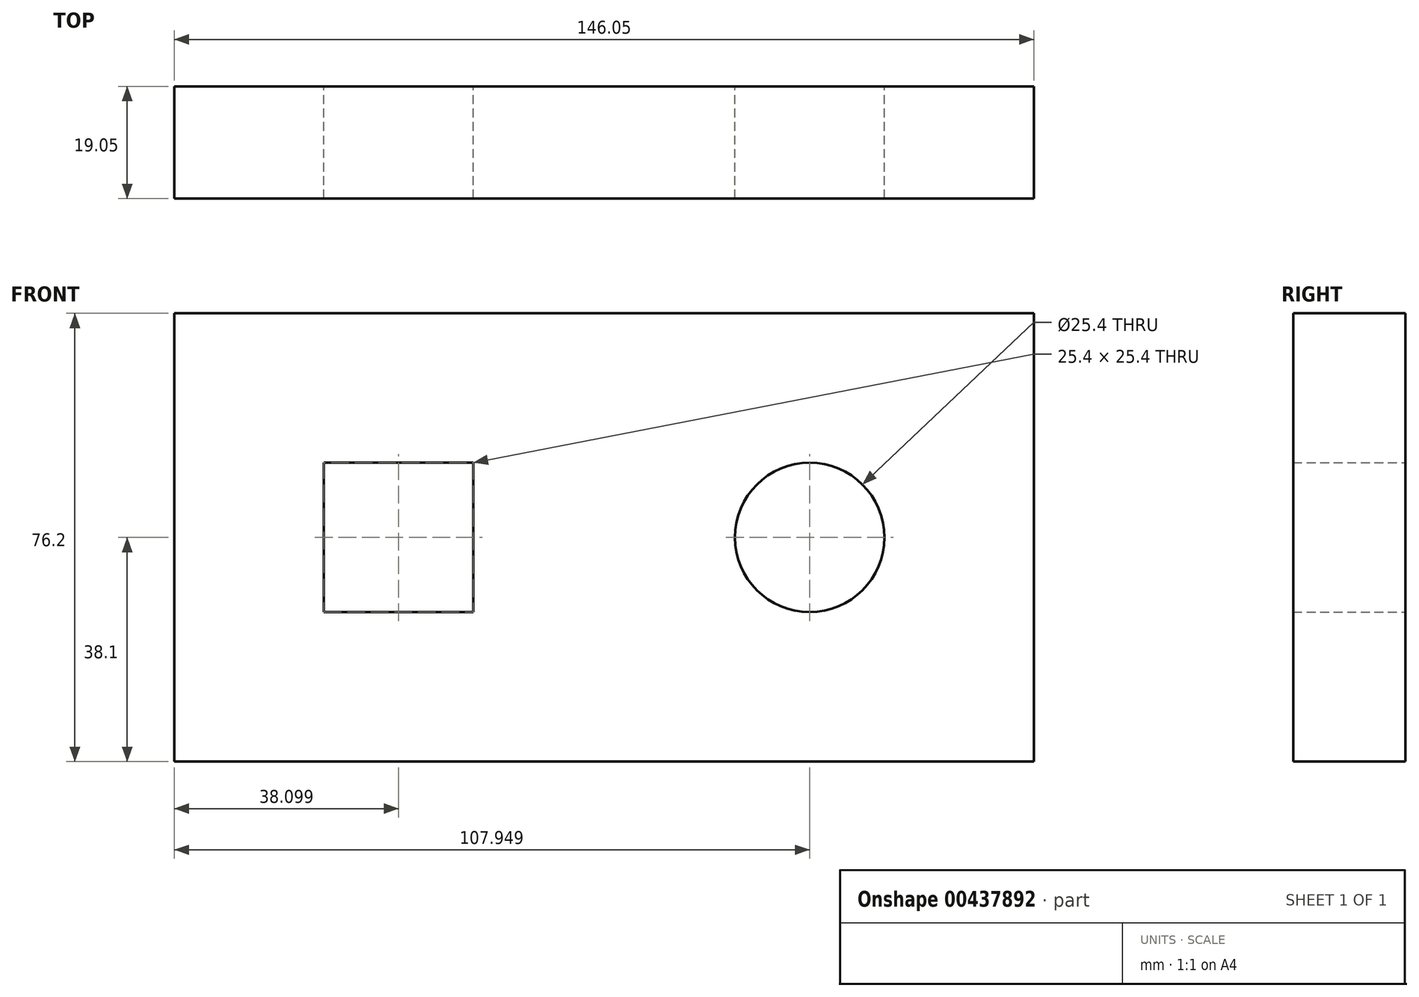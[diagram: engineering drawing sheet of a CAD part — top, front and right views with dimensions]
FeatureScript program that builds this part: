
annotation { "Feature Type Name" : "Feature", "Feature Type Description" : "" }
export const myFeature = defineFeature(function(context is Context, id is Id, definition is map)
    precondition{}
    {
        {
            var Q0;
            Q0=qCreatedBy(makeId("Front.planeOp"),FACE);
            var sketch = newSketch(context, id + "F0", { "sketchPlane" : qUnion([Q0])});
            skLineSegment(sketch, "E0", {"start": v(-64.16, 56.15) * mm, "end": v(-64.16, -20.05) * mm});
            skLineSegment(sketch, "E1", {"start": v(-64.16, 56.15) * mm, "end": v(81.89, 56.15) * mm});
            skLineSegment(sketch, "E2", {"start": v(81.89, 56.15) * mm, "end": v(81.89, -20.05) * mm});
            skLineSegment(sketch, "E3", {"start": v(81.89, -20.05) * mm, "end": v(-64.16, -20.05) * mm});
            skCircle(sketch, "E4", {"center": v(43.79, 18.05) * mm, "radius": 12.7 * mm});
            skLineSegment(sketch, "E5.bottom", {"start": v(-38.76, 30.75) * mm, "end": v(-13.36, 30.75) * mm});
            skLineSegment(sketch, "E5.top", {"start": v(-38.76, 5.35) * mm, "end": v(-13.36, 5.35) * mm});
            skLineSegment(sketch, "E5.left", {"start": v(-38.76, 30.75) * mm, "end": v(-38.76, 5.35) * mm});
            skLineSegment(sketch, "E5.right", {"start": v(-13.36, 30.75) * mm, "end": v(-13.36, 5.35) * mm});
            skSolve(sketch);
        }
        {
            var Q0;
            Q0=makeQuery(id+"F0.imprint","IMPRINT",FACE,{"disambiguationData":[TD([[makeQuery(id+"F0.imprint","IMPRINT",EDGE,{"derivedFrom":sQuery(id+"F0.wireOp",EDGE,"E0")}),1.0]])]});
            extrude(context, id + "F1", {"entities" : qUnion([Q0]), "depth" : 19.05 * mm});
        }
    });
